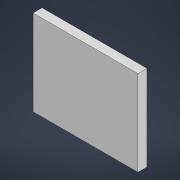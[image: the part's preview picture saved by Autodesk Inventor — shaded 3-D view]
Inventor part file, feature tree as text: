
AUTODESK INVENTOR PART (.ipt)
format: ipt  version: 2022 (Build 260153000, 153)  size: 82,944 bytes
history: native  units: mm
features: extrude x1, sketch x1
ambient origin geometry x8: Origin, YZ Plane, XZ Plane, XY Plane, X Axis, Y Axis, Z Axis, Center Point
bodies: Solid1 (feature_tree)
feature tree (2):
  extrude  "Extrusion1"  Depth=28.5mm
  sketch  "Sketch1"  dims[d0=35.0mm d1=28.5mm d2=3.0mm d3=0.0mm]
